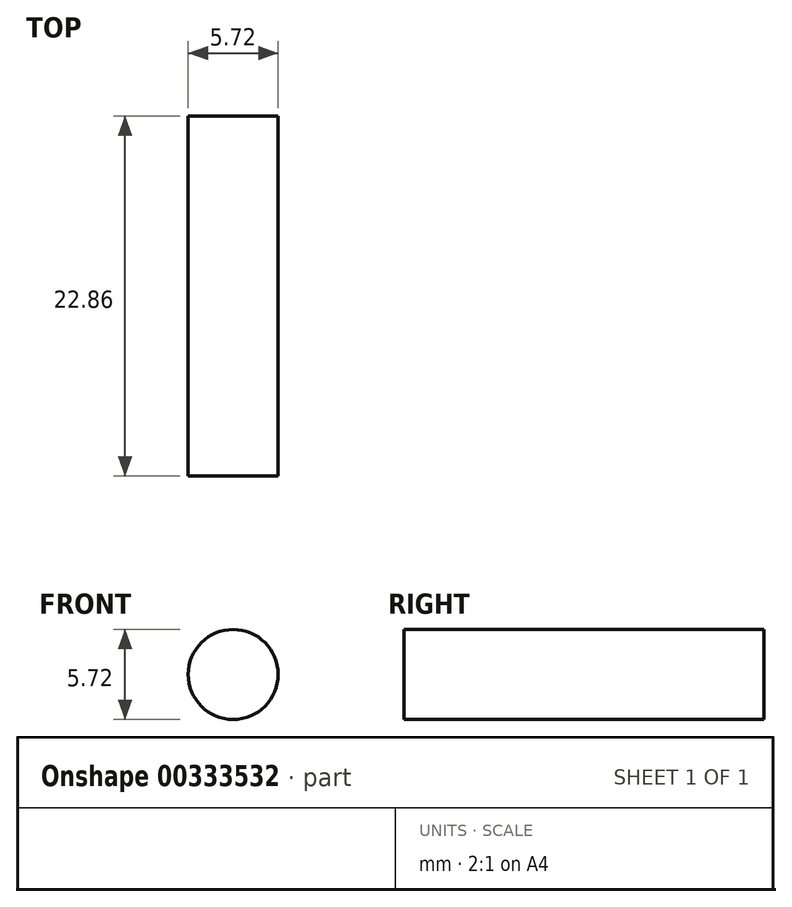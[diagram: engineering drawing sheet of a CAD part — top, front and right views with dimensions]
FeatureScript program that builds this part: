
annotation { "Feature Type Name" : "Feature", "Feature Type Description" : "" }
export const myFeature = defineFeature(function(context is Context, id is Id, definition is map)
    precondition{}
    {
        {
            var Q0;
            Q0=qCreatedBy(makeId("Front.planeOp"),FACE);
            var sketch = newSketch(context, id + "F0", { "sketchPlane" : qUnion([Q0])});
            skCircle(sketch, "E0", {"center": v(0, 0) * mm, "radius": 2.86 * mm});
            skSolve(sketch);
        }
        {
            var Q0;
            Q0 = qSketchRegion(id + "F0", true);
            extrude(context, id + "F1", {"entities" : qUnion([Q0]), "depth" : 22.86 * mm, "offsetDistance" : 25.4 * mm, "symmetric" : true});
        }
    });
